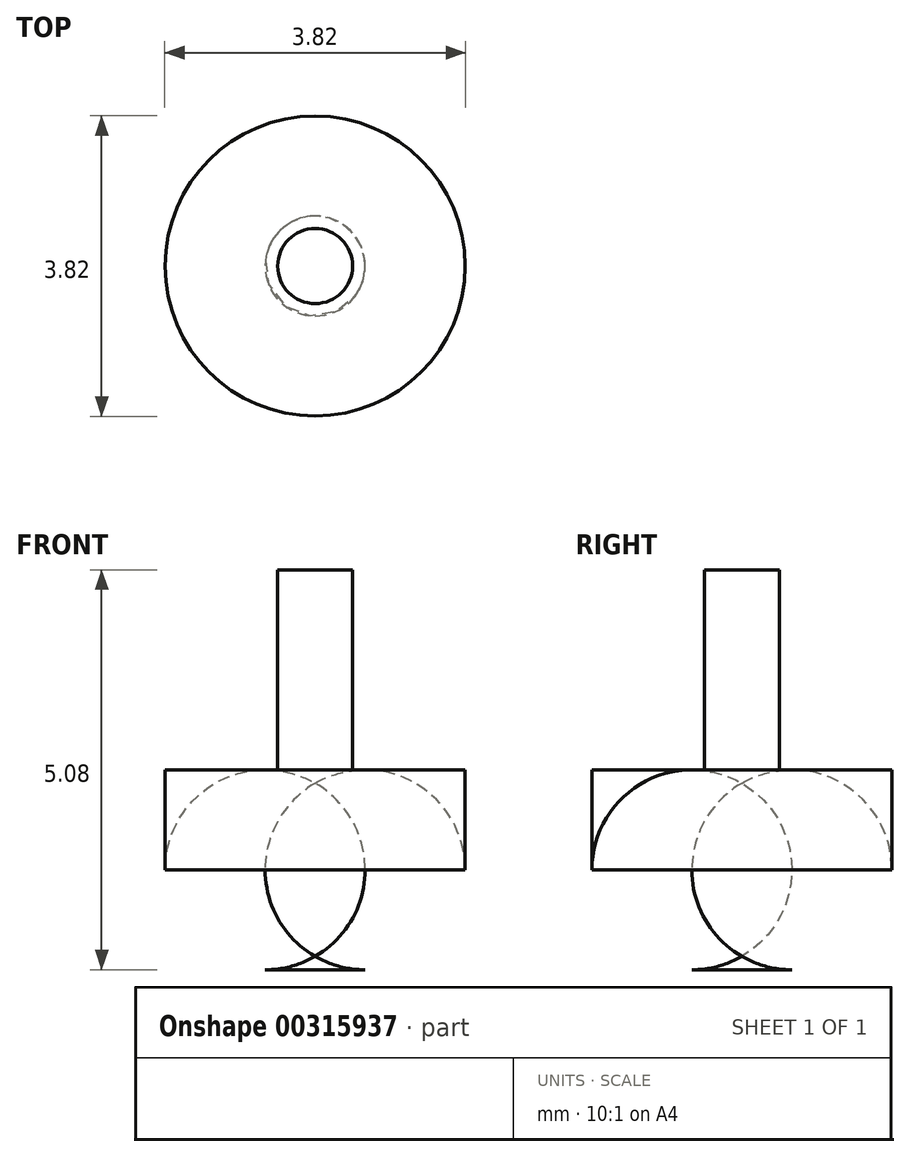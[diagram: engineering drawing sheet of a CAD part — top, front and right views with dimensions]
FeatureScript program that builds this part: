
annotation { "Feature Type Name" : "Feature", "Feature Type Description" : "" }
export const myFeature = defineFeature(function(context is Context, id is Id, definition is map)
    precondition{}
    {
        {
            var Q0;
            Q0=qCreatedBy(makeId("Top.planeOp"),FACE);
            var sketch = newSketch(context, id + "F0", { "sketchPlane" : qUnion([Q0])});
            skCircle(sketch, "E0", {"center": v(0, 0) * mm, "radius": 1.9 * mm});
            skCircle(sketch, "E1", {"center": v(0, 0) * mm, "radius": 0.48 * mm});
            skSolve(sketch);
        }
        {
            var Q0;
            Q0=makeQuery(id+"F0.imprint","IMPRINT",FACE,{"disambiguationData":[TD([[makeQuery(id+"F0.imprint","IMPRINT",EDGE,{"derivedFrom":sQuery(id+"F0.wireOp",EDGE,"E0")}),1.0]])]});
            extrude(context, id + "F1", {"entities" : qUnion([Q0]), "depth" : 2.54 * mm});
        }
        {
            var Q0;
            Q0=makeQuery(id+"F0.imprint","IMPRINT",FACE,{"disambiguationData":[TD([[makeQuery(id+"F0.imprint","IMPRINT",EDGE,{"derivedFrom":sQuery(id+"F0.wireOp",EDGE,"E1")}),1.0]])]});
            extrude(context, id + "F2", {"entities" : qUnion([Q0]), "operationType" : NewBodyOperationType.ADD, "depth" : 5.08 * mm});
        }
        {
            var Q0;
            Q0=qCreatedBy(makeId("Front.planeOp"),FACE);
            var sketch = newSketch(context, id + "F3", { "sketchPlane" : qUnion([Q0])});
            skCircle(sketch, "E2", {"center": v(8.7, 1.08) * mm, "radius": 2.59 * mm});
            skSolve(sketch);
        }
        {
            var Q0;
            Q0=makeQuery(id+"F1.opExtrude","CAP_EDGE",EDGE,{"disambiguationData":[OSD([sQuery(id+"F0.wireOp",EDGE,"E0")])],"isStart":true});
            fillet(context, id + "F4", {"entities" : qUnion([Q0]), "radius" : 1.27 * mm, "tangentPropagation" : true, "allowEdgeOverflow" : false});
        }
        {
            var Q0;
            Q0=makeQuery(id+"F3.imprint","IMPRINT",FACE,{"disambiguationData":[TD([[makeQuery(id+"F3.imprint","IMPRINT",EDGE,{"derivedFrom":sQuery(id+"F3.wireOp",EDGE,"E2")}),1.0]])]});
            extrude(context, id + "F5", {"entities" : qUnion([Q0]), "operationType" : NewBodyOperationType.REMOVE, "endBound" : BoundingType.THROUGH_ALL, "oppositeDirection" : true, "depth" : 25.4 * mm});
        }
        {
            var Q0;
            Q0=qSketchRegion(id+"F3",true);
            extrude(context, id + "F6", {"entities" : qUnion([Q0]), "operationType" : NewBodyOperationType.REMOVE, "depth" : 25.4 * mm});
        }
        {
            var Q0;
            Q0=makeQuery(id+"F1.opExtrude","SWEPT_BODY",BODY,{"disambiguationData":[OSD([sQuery(id+"F0.wireOp",EDGE,"E0"),sQuery(id+"F0.wireOp",EDGE,"E1")])]});
            var Q1;
            Q1=makeQuery(id+"F2.opExtrude","SWEPT_FACE",FACE,{"disambiguationData":[OSD([sQuery(id+"F0.wireOp",EDGE,"E1")])]});
            transform(context, id + "F7", {"entities" : qUnion([Q0]), "transformType" : TransformType.ROTATION, "transformAxis" : qUnion([Q1]), "angle" : 90 * degree, "makeCopy" : false});
        }
    });
